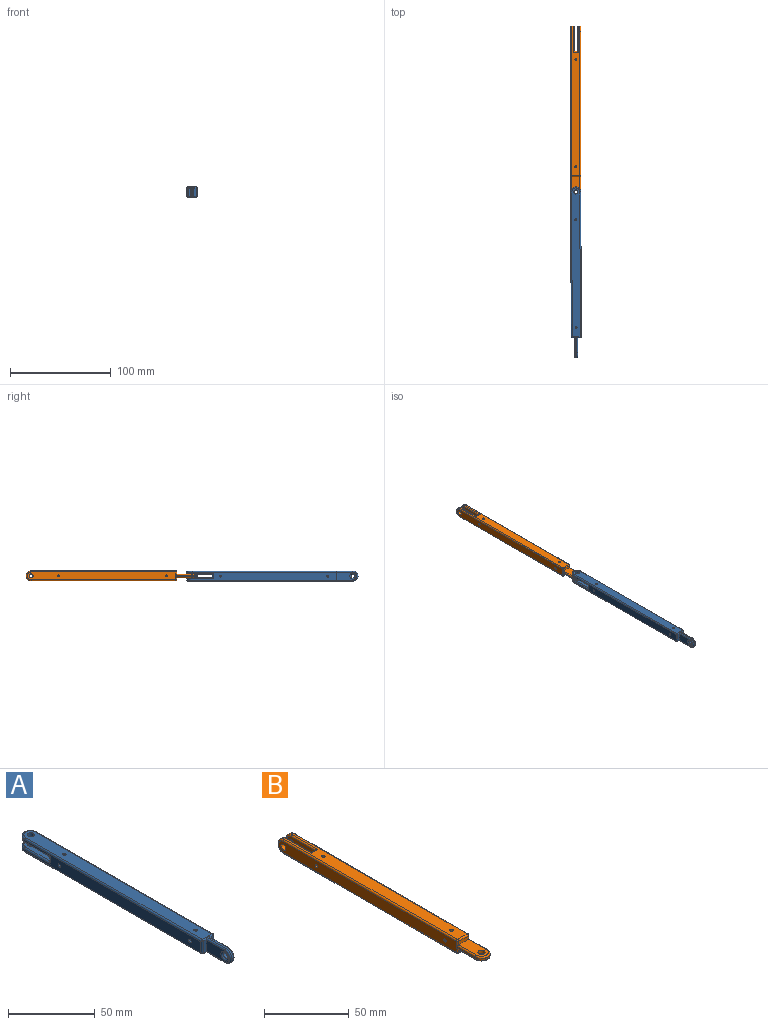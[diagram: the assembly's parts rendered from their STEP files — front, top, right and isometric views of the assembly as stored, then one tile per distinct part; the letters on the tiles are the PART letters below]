
ASSEMBLY  parts=2 mates=1
PART A: 52 faces, bbox 10.8x170.8x10.8 mm
  f0: cylinder r=1mm len=10mm, axis (0,0,1), area 56.8mm2, adj f3,f5,f20
  f1: plane 144x8mm, normal (-1,0,0), area 1032.3mm2, adj f12,f14,f19,f20,f24,f30,f37,f46
  f2: plane 8x2.4mm, normal (0,-1,0), area 19.2mm2, adj f7,f32,f38,f39
  f3: plane 164x8mm, normal (0,0,-1), area 1177.5mm2, adj f0,f13,f17,f18,f21,f23,f24,f27
  f4: plane 144x8mm, normal (1,0,0), area 1032.3mm2, adj f12,f14,f19,f20,f31,f38,f42,f43
  f5: plane 164x8mm, normal (0,0,1), area 1177.5mm2, adj f0,f13,f16,f18,f25,f29,f36,f37
  f6: plane 8x2.4mm, normal (0,-1,0), area 19.2mm2, adj f8,f23,f29,f30
  f7: plane 19x8mm, normal (1,0,0), area 131.3mm2, adj f2,f15,f28,f33,f36
  f8: plane 19x8mm, normal (-1,0,0), area 114.9mm2, adj f6,f21,f22,f25,f51
  f9: plane 24x8mm, normal (0,0,1), area 172.6mm2, adj f11,f17,f43,f44,f46
  f10: plane 24x8mm, normal (0,0,-1), area 172.6mm2, adj f11,f16,f47,f49,f50
  f11: plane 8x3.4mm, normal (0,1,0), area 27.2mm2, adj f9,f10,f45,f48
  f12: cylinder r=5mm len=10mm, axis (0,0,1), area 20.4mm2, adj f1,f4,f27,f44
  f13: cylinder r=5mm len=10mm, axis (1,0,0), area 18.8mm2, adj f3,f5,f22,f33
  f14: cylinder r=5mm len=10mm, axis (0,0,-1), area 20.4mm2, adj f1,f4,f40,f49
  f15: cylinder r=2.1mm len=4.2mm, axis (-1,0,0), area 29mm2, adj f7,f51
  f16: cylinder r=2mm len=4mm, axis (0,0,1), area 41.5mm2, adj f5,f10
  f17: cylinder r=2mm len=4mm, axis (0,0,1), area 41.5mm2, adj f3,f9
  f18: cylinder r=1mm len=10mm, axis (0,0,1), area 55.4mm2, adj f3,f5,f19
  f19: cylinder r=1mm len=10mm, axis (1,0,0), area 55.4mm2, adj f1,f4,f18
  f20: cylinder r=1mm len=10mm, axis (1,0,0), area 56.8mm2, adj f0,f1,f4
  f21: cylinder r=1mm len=16mm, axis (0,1,0), area 24.1mm2, adj f3,f8,f22,f23
  f22: torus R=4mm, axis (1,0,0), area 22.9mm2, adj f8,f13,f21,f25
  f23: cylinder r=1mm len=3.4mm, axis (1,0,0), area 4.3mm2, adj f3,f6,f21,f26
  f24: cylinder r=1mm len=144mm, axis (0,1,0), area 226.2mm2, adj f1,f3,f26,f27
  f25: cylinder r=1mm len=16mm, axis (0,-1,0), area 24.1mm2, adj f5,f8,f22,f29
  f26: sphere r=1mm, area 1.6mm2, adj f23,f24,f30
  f27: torus R=4mm, axis (0,0,1), area 22.9mm2, adj f3,f12,f24,f31
  f28: cylinder r=1mm len=16mm, axis (0,-1,0), area 24.1mm2, adj f3,f7,f32,f33
  f29: cylinder r=1mm len=3.4mm, axis (-1,0,0), area 4.3mm2, adj f5,f6,f25,f34
  f30: cylinder r=1mm len=8mm, axis (0,0,-1), area 12.6mm2, adj f1,f6,f26,f34
  f31: cylinder r=1mm len=144mm, axis (0,-1,0), area 226.2mm2, adj f3,f4,f27,f35
  f32: cylinder r=1mm len=3.4mm, axis (1,0,0), area 4.3mm2, adj f2,f3,f28,f35
  f33: torus R=4mm, axis (1,0,0), area 22.9mm2, adj f7,f13,f28,f36
  f34: sphere r=1mm, area 1.6mm2, adj f29,f30,f37
  f35: sphere r=1mm, area 1.6mm2, adj f31,f32,f38
  f36: cylinder r=1mm len=16mm, axis (0,1,0), area 24.1mm2, adj f5,f7,f33,f39
  f37: cylinder r=1mm len=144mm, axis (0,-1,0), area 226.2mm2, adj f1,f5,f34,f40
  f38: cylinder r=1mm len=8mm, axis (0,0,1), area 12.6mm2, adj f2,f4,f35,f41
  f39: cylinder r=1mm len=3.4mm, axis (-1,0,0), area 4.3mm2, adj f2,f5,f36,f41
  f40: torus R=4mm, axis (0,0,1), area 22.9mm2, adj f5,f14,f37,f42
  f41: sphere r=1mm, area 1.6mm2, adj f38,f39,f42
  f42: cylinder r=1mm len=144mm, axis (0,1,0), area 226.2mm2, adj f4,f5,f40,f41
  f43: cylinder r=1mm len=21mm, axis (0,-1,0), area 32mm2, adj f4,f9,f44,f45
  f44: torus R=4mm, axis (0,0,1), area 22.9mm2, adj f9,f12,f43,f46
  f45: cylinder r=1mm len=5.4mm, axis (0,0,-1), area 6.5mm2, adj f4,f11,f43,f47
  f46: cylinder r=1mm len=21mm, axis (0,1,0), area 32mm2, adj f1,f9,f44,f48
  f47: cylinder r=1mm len=21mm, axis (0,1,0), area 32mm2, adj f4,f10,f45,f49
  f48: cylinder r=1mm len=5.4mm, axis (0,0,1), area 6.5mm2, adj f1,f11,f46,f50
  f49: torus R=4mm, axis (0,0,1), area 22.9mm2, adj f10,f14,f47,f50
  f50: cylinder r=1mm len=21mm, axis (0,-1,0), area 32mm2, adj f1,f10,f48,f49
  f51: torus R=3.1mm, axis (1,0,0), area 24.3mm2, adj f8,f15
PART B: 52 faces, bbox 10.8x170.8x10.8 mm
  f0: cylinder r=1mm len=10mm, axis (-1,0,0), area 56.8mm2, adj f3,f5,f20
  f1: plane 144x8mm, normal (0,0,-1), area 1032.3mm2, adj f12,f14,f19,f20,f24,f30,f37,f46
  f2: plane 8x2.4mm, normal (0,-1,0), area 19.2mm2, adj f7,f32,f38,f39
  f3: plane 164x8mm, normal (1,0,0), area 1177.5mm2, adj f0,f13,f17,f18,f21,f23,f24,f27
  f4: plane 144x8mm, normal (0,0,1), area 1032.3mm2, adj f12,f14,f19,f20,f31,f38,f42,f43
  f5: plane 164x8mm, normal (-1,0,0), area 1177.5mm2, adj f0,f13,f16,f18,f25,f29,f36,f37
  f6: plane 8x2.4mm, normal (0,-1,0), area 19.2mm2, adj f8,f23,f29,f30
  f7: plane 19x8mm, normal (0,0,1), area 131.3mm2, adj f2,f15,f28,f33,f36
  f8: plane 19x8mm, normal (0,0,-1), area 114.9mm2, adj f6,f21,f22,f25,f51
  f9: plane 24x8mm, normal (-1,0,0), area 172.6mm2, adj f11,f17,f43,f44,f46
  f10: plane 24x8mm, normal (1,0,0), area 172.6mm2, adj f11,f16,f47,f49,f50
  f11: plane 8x3.4mm, normal (0,1,0), area 27.2mm2, adj f9,f10,f45,f48
  f12: cylinder r=5mm len=10mm, axis (-1,0,0), area 20.4mm2, adj f1,f4,f27,f44
  f13: cylinder r=5mm len=10mm, axis (0,0,1), area 18.8mm2, adj f3,f5,f22,f33
  f14: cylinder r=5mm len=10mm, axis (1,0,0), area 20.4mm2, adj f1,f4,f40,f49
  f15: cylinder r=2.1mm len=4.2mm, axis (0,0,-1), area 29mm2, adj f7,f51
  f16: cylinder r=2mm len=4mm, axis (-1,0,0), area 41.5mm2, adj f5,f10
  f17: cylinder r=2mm len=4mm, axis (-1,0,0), area 41.5mm2, adj f3,f9
  f18: cylinder r=1mm len=10mm, axis (-1,0,0), area 55.4mm2, adj f3,f5,f19
  f19: cylinder r=1mm len=10mm, axis (0,0,1), area 55.4mm2, adj f1,f4,f18
  f20: cylinder r=1mm len=10mm, axis (0,0,1), area 56.8mm2, adj f0,f1,f4
  f21: cylinder r=1mm len=16mm, axis (0,1,0), area 24.1mm2, adj f3,f8,f22,f23
  f22: torus R=4mm, axis (0,0,1), area 22.9mm2, adj f8,f13,f21,f25
  f23: cylinder r=1mm len=3.4mm, axis (0,0,1), area 4.3mm2, adj f3,f6,f21,f26
  f24: cylinder r=1mm len=144mm, axis (0,1,0), area 226.2mm2, adj f1,f3,f26,f27
  f25: cylinder r=1mm len=16mm, axis (0,-1,0), area 24.1mm2, adj f5,f8,f22,f29
  f26: sphere r=1mm, area 1.6mm2, adj f23,f24,f30
  f27: torus R=4mm, axis (-1,0,0), area 22.9mm2, adj f3,f12,f24,f31
  f28: cylinder r=1mm len=16mm, axis (0,-1,0), area 24.1mm2, adj f3,f7,f32,f33
  f29: cylinder r=1mm len=3.4mm, axis (0,0,-1), area 4.3mm2, adj f5,f6,f25,f34
  f30: cylinder r=1mm len=8mm, axis (1,0,0), area 12.6mm2, adj f1,f6,f26,f34
  f31: cylinder r=1mm len=144mm, axis (0,-1,0), area 226.2mm2, adj f3,f4,f27,f35
  f32: cylinder r=1mm len=3.4mm, axis (0,0,1), area 4.3mm2, adj f2,f3,f28,f35
  f33: torus R=4mm, axis (0,0,1), area 22.9mm2, adj f7,f13,f28,f36
  f34: sphere r=1mm, area 1.6mm2, adj f29,f30,f37
  f35: sphere r=1mm, area 1.6mm2, adj f31,f32,f38
  f36: cylinder r=1mm len=16mm, axis (0,1,0), area 24.1mm2, adj f5,f7,f33,f39
  f37: cylinder r=1mm len=144mm, axis (0,-1,0), area 226.2mm2, adj f1,f5,f34,f40
  f38: cylinder r=1mm len=8mm, axis (-1,0,0), area 12.6mm2, adj f2,f4,f35,f41
  f39: cylinder r=1mm len=3.4mm, axis (0,0,-1), area 4.3mm2, adj f2,f5,f36,f41
  f40: torus R=4mm, axis (-1,0,0), area 22.9mm2, adj f5,f14,f37,f42
  f41: sphere r=1mm, area 1.6mm2, adj f38,f39,f42
  f42: cylinder r=1mm len=144mm, axis (0,1,0), area 226.2mm2, adj f4,f5,f40,f41
  f43: cylinder r=1mm len=21mm, axis (0,-1,0), area 32mm2, adj f4,f9,f44,f45
  f44: torus R=4mm, axis (-1,0,0), area 22.9mm2, adj f9,f12,f43,f46
  f45: cylinder r=1mm len=5.4mm, axis (1,0,0), area 6.5mm2, adj f4,f11,f43,f47
  f46: cylinder r=1mm len=21mm, axis (0,1,0), area 32mm2, adj f1,f9,f44,f48
  f47: cylinder r=1mm len=21mm, axis (0,1,0), area 32mm2, adj f4,f10,f45,f49
  f48: cylinder r=1mm len=5.4mm, axis (-1,0,0), area 6.5mm2, adj f1,f11,f46,f50
  f49: torus R=4mm, axis (-1,0,0), area 22.9mm2, adj f10,f14,f47,f50
  f50: cylinder r=1mm len=21mm, axis (0,-1,0), area 32mm2, adj f1,f10,f48,f49
  f51: torus R=3.1mm, axis (0,0,1), area 24.3mm2, adj f8,f15
PLACE A rot(axis=(0,0,1),0.1deg) t=(-122.56,-135.9,16.68)mm
PLACE B rot(axis=(0,0,-1),0deg) t=(-122.82,44.1,36.78)mm fixed
MATE revolute B.f15 <-> A.f16  axis (0,0,1) through (-122.82,29.1,38.38)mm
